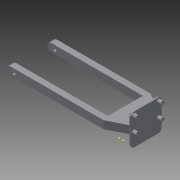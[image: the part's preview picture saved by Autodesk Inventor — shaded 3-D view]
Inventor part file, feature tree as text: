
AUTODESK INVENTOR PART (.ipt)
format: ipt  version: 2015 (Build 190159000, 159)  size: 225,280 bytes
history: native  units: in
note: dims shown in document units (in); Inventor stores cm internally (conversion verified against a paired STEP export)
features: fillet x14, sketch x11, extrude x7, thread x4
ambient origin geometry x8: Origin, YZ Plane, XZ Plane, XY Plane, X Axis, Y Axis, Z Axis, Center Point
bodies: Solid1 (feature_tree)
feature tree (36):
  extrude  "Extrusion1"  Depth=0.1879in
  extrude  "Extrusion2"  Depth=1.125in
  sketch  "Sketch3"  dims[d4=0.1875in d5=3.625in]
  extrude  "Extrusion3"  Depth=3.625in
  extrude  "Extrusion4"  Depth=0.12in
  extrude  "Extrusion5"  Depth=0.065in
  extrude  "Extrusion6"  Depth=0.125in
  fillet  "Fillet1"  Radius=1.0in
  fillet  "Fillet2"  Radius=1.0in
  fillet  "Fillet3"  Radius=0.25in
  fillet  "Fillet4"  Radius=0.375in
  fillet  "Fillet5"  Radius=0.125in
  fillet  "Fillet6"  Radius=0.5in
  fillet  "Fillet7"  Radius=0.25in
  fillet  "Fillet8"  Radius=0.5in
  fillet  "Fillet9"  Radius=0.25in
  fillet  "Fillet10"  Radius=0.125in
  fillet  "Fillet11"  Radius=0.125in
  fillet  "Fillet12"  Radius=0.125in
  fillet  "Fillet13"  Radius=0.125in
  fillet  "Fillet14"  Radius=0.1in
  extrude  "Extrusion7"  Depth=0.1in
  thread  "Thread1"  [1 undecoded]
  thread  "Thread2"  [1 undecoded]
  thread  "Thread3"  [1 undecoded]
  thread  "Thread4"  [1 undecoded]
  sketch  "Sketch9"  dims[d39=0.125in d40=0.0in]
  sketch  "Sketch10"  dims[d41=0.125in]
  sketch  "Sketch11"  dims[d42=0.125in d43=0.125in d44=0.125in d45=0.125in d46=0.125in d47=0.125in d48=0.125in d49=0.125in d50=0.125in d51=0.125in d52=0.125in d53=0.125in d54=0.125in d55=0.08in d56=0.08in d57=0.08in d58=0.08in d59=0.125in d60=0.0in d61=1.0in d62=0.0in d63=1.0in d64=0.0in d65=1.0in d66=0.0in d67=1.0in d68=0.0in]
  sketch  "Sketch1"  dims[d0=3.625in d1=0.1879in]
  sketch  "Sketch2"  dims[d2=3.0in d3=1.125in]
  sketch  "Sketch4"  dims[d6=0.25in d7=0.0in d8=0.12in]
  sketch  "Sketch5"  dims[d10=0.065in d11=0.15in]
  sketch  "Sketch6"  dims[d12=1.7in d13=0.0in d14=1.0in d15=1.0in d16=1.0in d17=0.25in d18=0.375in d19=0.125in d20=0.0in d21=0.5in d22=0.25in d23=0.0in d24=0.5in d25=0.25in d26=0.0in d27=0.125in d28=0.125in d29=0.125in d30=0.125in d31=0.1in]
  sketch  "Sketch7"  dims[d32=0.1in d33=0.1in d34=0.1in d35=0.1in d36=0.1in d37=0.5625in]
  sketch  "Sketch8"  dims[d38=0.5625in]
note: 4 required parameter values undecoded (feature->parameter linkage not recoverable at this tier; creation-order binding heuristic only, values carry confidence <= 0.55)
